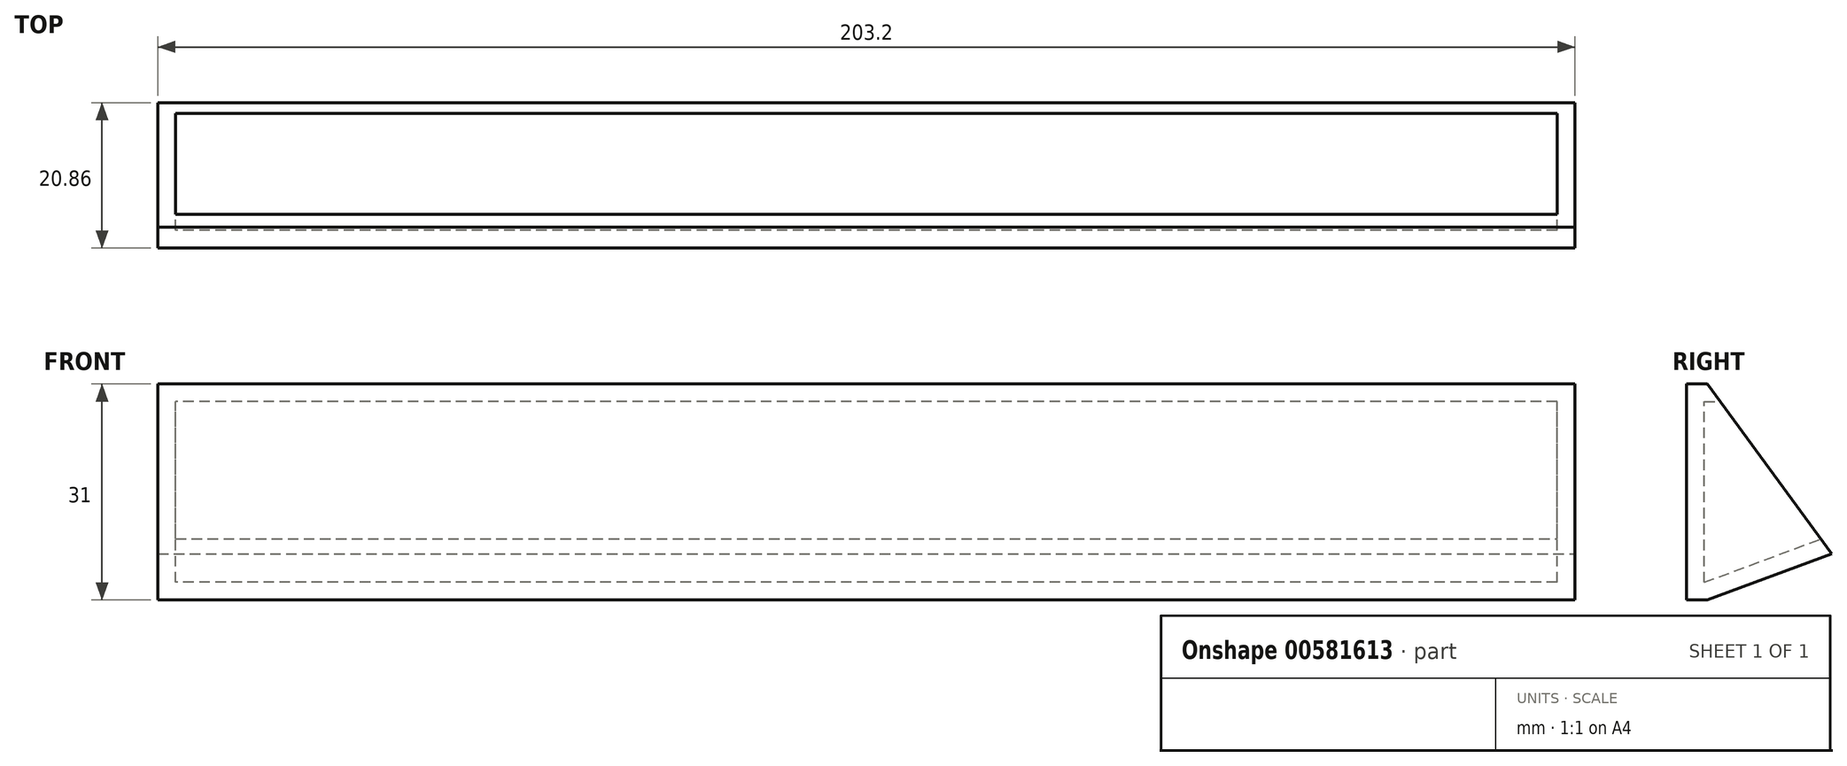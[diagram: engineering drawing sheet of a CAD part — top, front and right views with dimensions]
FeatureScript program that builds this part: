
annotation { "Feature Type Name" : "Feature", "Feature Type Description" : "" }
export const myFeature = defineFeature(function(context is Context, id is Id, definition is map)
    precondition{}
    {
        {
            var Q0;
            Q0=qCreatedBy(makeId("Front.planeOp"),FACE);
            var sketch = newSketch(context, id + "F0", { "sketchPlane" : qUnion([Q0])});
            skLineSegment(sketch, "E0.bottom", {"start": v(0, 0) * mm, "end": v(-203.2, 0) * mm});
            skLineSegment(sketch, "E0.top", {"start": v(0, 31) * mm, "end": v(-203.2, 31) * mm});
            skLineSegment(sketch, "E0.left", {"start": v(0, 0) * mm, "end": v(0, 31) * mm});
            skLineSegment(sketch, "E0.right", {"start": v(-203.2, 0) * mm, "end": v(-203.2, 31) * mm});
            skSolve(sketch);
        }
        {
            var Q0;
            Q0 = qSketchRegion(id + "F0", true);
            extrude(context, id + "F1", {"entities" : qUnion([Q0]), "depth" : 3 * mm, "offsetDistance" : 25.4 * mm});
        }
        {
            var Q0;
            Q0=makeQuery(id+"F1.opExtrude","SWEPT_FACE",FACE,{"disambiguationData":[OSD([sQuery(id+"F0.wireOp",EDGE,"E0.left")])]});
            var sketch = newSketch(context, id + "F2", { "sketchPlane" : qUnion([Q0])});
            skLineSegment(sketch, "E1", {"start": v(0, 0) * mm, "end": v(17.86, 6.64) * mm});
            skLineSegment(sketch, "E2", {"start": v(17.86, 6.64) * mm, "end": v(0, 31) * mm});
            skLineSegment(sketch, "E3", {"start": v(0, 31) * mm, "end": v(0, 0) * mm});
            skSolve(sketch);
        }
        {
            var Q0;
            Q0 = qSketchRegion(id + "F2", true);
            extrude(context, id + "F3", {"entities" : qUnion([Q0]), "operationType" : NewBodyOperationType.ADD, "oppositeDirection" : true, "depth" : 203.2 * mm, "offsetDistance" : 25.4 * mm});
        }
        {
            var Q0;
            Q0=makeQuery(id+"F3.opExtrude","SWEPT_FACE",FACE,{"disambiguationData":[OSD([sQuery(id+"F2.wireOp",EDGE,"E2")])]});
            shell(context, id + "F4", {"entities" : qUnion([Q0]), "thickness" : 2.54 * mm});
        }
    });
